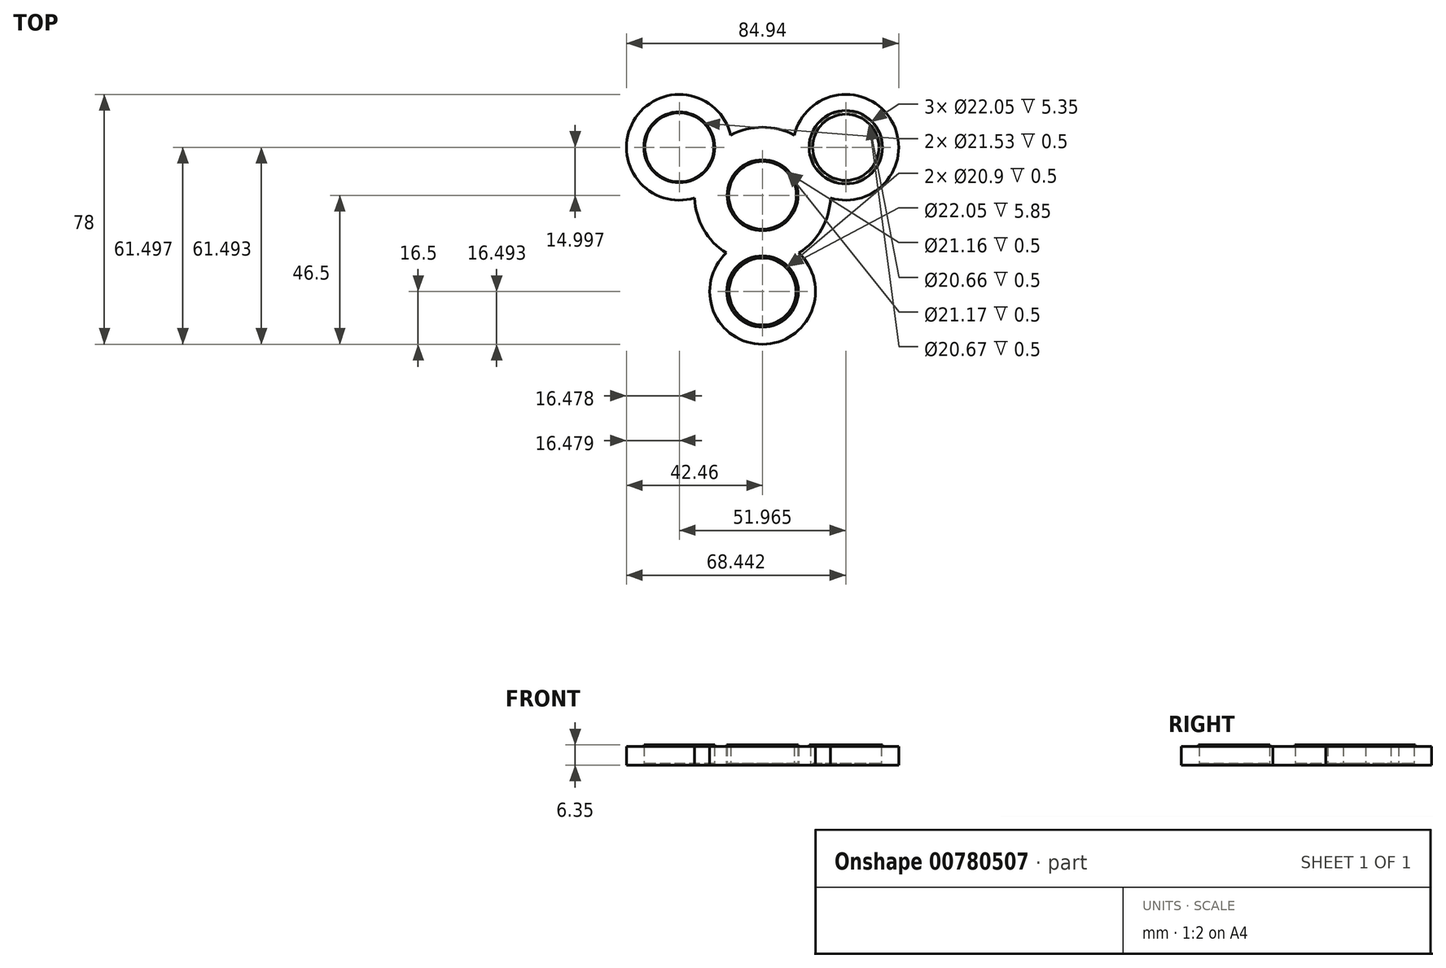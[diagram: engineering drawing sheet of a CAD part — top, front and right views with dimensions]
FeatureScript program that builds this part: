
annotation { "Feature Type Name" : "Feature", "Feature Type Description" : "" }
export const myFeature = defineFeature(function(context is Context, id is Id, definition is map)
    precondition{}
    {
        {
            var Q0;
            Q0=qCreatedBy(makeId("Top.planeOp"),FACE);
            var sketch = newSketch(context, id + "F0", { "sketchPlane" : qUnion([Q0])});
            skCircle(sketch, "E0", {"center": v(-25.96, 14.97) * mm, "radius": 16.5 * mm});
            skCircle(sketch, "E1", {"center": v(25.98, 15) * mm, "radius": 16.5 * mm});
            skCircle(sketch, "E2", {"center": v(0, -30) * mm, "radius": 16.5 * mm});
            skArc(sketch, "E3", {"start": v(-21.23, -0.84) * mm, "mid": v(-18.39, -10.63) * mm, "end": v(-11.31, -17.98) * mm});
            skArc(sketch, "E4.trimOffspring", {"start": v(11.31, -17.98) * mm, "mid": v(18.4, -10.62) * mm, "end": v(21.23, -0.8) * mm});
            skArc(sketch, "E5.trimOffspring", {"start": v(9.92, 18.78) * mm, "mid": v(0, 21.24) * mm, "end": v(-9.91, 18.79) * mm});
            skSolve(sketch);
        }
        {
            var Q0;
            Q0=qCreatedBy(makeId("Top.planeOp"),FACE);
            var sketch = newSketch(context, id + "F1", { "sketchPlane" : qUnion([Q0])});
            skCircle(sketch, "E6", {"center": v(0, 0) * mm, "radius": 11.03 * mm});
            skCircle(sketch, "E7", {"center": v(25.98, 15) * mm, "radius": 11.03 * mm});
            skCircle(sketch, "E8", {"center": v(-25.98, 15) * mm, "radius": 11.03 * mm});
            skCircle(sketch, "E9", {"center": v(0, -30) * mm, "radius": 11.03 * mm});
            skSolve(sketch);
        }
        {
            var Q0;
            Q0 = qSketchRegion(id + "F0", true);
            extrude(context, id + "F2", {"entities" : qUnion([Q0]), "depth" : 5.85 * mm, "offsetDistance" : 25 * mm});
        }
        {
            var Q0;
            Q0 = qSketchRegion(id + "F1", true);
            extrude(context, id + "F3", {"entities" : qUnion([Q0]), "operationType" : NewBodyOperationType.REMOVE, "depth" : 6.85 * mm, "offsetDistance" : 25 * mm});
        }
        {
            var Q0;
            Q0=makeQuery(id+"F1.imprint","IMPRINT",FACE,{"disambiguationData":[TD([[makeQuery(id+"F1.imprint","IMPRINT",EDGE,{"derivedFrom":sQuery(id+"F1.wireOp",EDGE,"E8")}),1.0]])]});
            var sketch = newSketch(context, id + "F4", { "sketchPlane" : qUnion([Q0])});
            skCircle(sketch, "E10", {"center": v(-25.98, 15) * mm, "radius": 11.04 * mm});
            skCircle(sketch, "E11", {"center": v(-25.98, 15) * mm, "radius": 10.76 * mm});
            skSolve(sketch);
        }
        {
            var Q0;
            Q0 = qSketchRegion(id + "F4", true);
            extrude(context, id + "F5", {"entities" : qUnion([Q0]), "operationType" : NewBodyOperationType.ADD, "depth" : .5 * mm, "offsetDistance" : 25 * mm});
        }
        {
            var Q0;
            Q0=makeQuery(id+"F1.imprint","IMPRINT",FACE,{"disambiguationData":[TD([[makeQuery(id+"F1.imprint","IMPRINT",EDGE,{"derivedFrom":sQuery(id+"F1.wireOp",EDGE,"E6")}),1.0]])]});
            var sketch = newSketch(context, id + "F6", { "sketchPlane" : qUnion([Q0])});
            skCircle(sketch, "E12", {"center": v(0, 0) * mm, "radius": 11.04 * mm});
            skCircle(sketch, "E13", {"center": v(0, 0) * mm, "radius": 10.58 * mm});
            skSolve(sketch);
        }
        {
            var Q0;
            Q0 = qSketchRegion(id + "F6", true);
            extrude(context, id + "F7", {"entities" : qUnion([Q0]), "operationType" : NewBodyOperationType.ADD, "depth" : .5 * mm, "offsetDistance" : 25 * mm});
        }
        {
            var Q0;
            Q0=makeQuery(id+"F1.imprint","IMPRINT",FACE,{"disambiguationData":[TD([[makeQuery(id+"F1.imprint","IMPRINT",EDGE,{"derivedFrom":sQuery(id+"F1.wireOp",EDGE,"E7")}),1.0]])]});
            var sketch = newSketch(context, id + "F8", { "sketchPlane" : qUnion([Q0])});
            skCircle(sketch, "E14", {"center": v(25.98, 15) * mm, "radius": 11.03 * mm});
            skCircle(sketch, "E15", {"center": v(25.98, 15) * mm, "radius": 10.33 * mm});
            skSolve(sketch);
        }
        {
            var Q0;
            Q0 = qSketchRegion(id + "F8", true);
            extrude(context, id + "F9", {"entities" : qUnion([Q0]), "operationType" : NewBodyOperationType.ADD, "depth" : .5 * mm, "offsetDistance" : 25 * mm});
        }
        {
            var Q0;
            Q0=makeQuery(id+"F1.imprint","IMPRINT",FACE,{"disambiguationData":[TD([[makeQuery(id+"F1.imprint","IMPRINT",EDGE,{"derivedFrom":sQuery(id+"F1.wireOp",EDGE,"E9")}),1.0]])]});
            var sketch = newSketch(context, id + "F10", { "sketchPlane" : qUnion([Q0])});
            skCircle(sketch, "E16", {"center": v(0, -30) * mm, "radius": 11.02 * mm});
            skCircle(sketch, "E17", {"center": v(0, -30) * mm, "radius": 10.45 * mm});
            skSolve(sketch);
        }
        {
            var Q0;
            Q0 = qSketchRegion(id + "F10", true);
            extrude(context, id + "F11", {"entities" : qUnion([Q0]), "operationType" : NewBodyOperationType.ADD, "depth" : .5 * mm, "offsetDistance" : 25 * mm});
        }
        {
            var Q0;
            Q0=makeQuery(id+"F2.opExtrude","CAP_FACE",FACE,{"disambiguationData":[OSD([sQuery(id+"F0.wireOp",EDGE,"E0"),sQuery(id+"F0.wireOp",EDGE,"E1"),sQuery(id+"F0.wireOp",EDGE,"E2"),sQuery(id+"F0.wireOp",EDGE,"E3"),sQuery(id+"F0.wireOp",EDGE,"E4.trimOffspring"),sQuery(id+"F0.wireOp",EDGE,"E5.trimOffspring")])],"isStart":false});
            var sketch = newSketch(context, id + "F12", { "sketchPlane" : qUnion([Q0])});
            skCircle(sketch, "E18.0", {"center": v(-25.98, 15) * mm, "radius": 11.05 * mm});
            skCircle(sketch, "E19.0", {"center": v(-25.98, 15) * mm, "radius": 10.76 * mm});
            skCircle(sketch, "E20.0", {"center": v(25.98, 15) * mm, "radius": 10.33 * mm});
            skCircle(sketch, "E21.0", {"center": v(0, 0) * mm, "radius": 10.58 * mm});
            skCircle(sketch, "E22.0", {"center": v(0, -30) * mm, "radius": 10.45 * mm});
            skCircle(sketch, "E23", {"center": v(0, 0) * mm, "radius": 11.06 * mm});
            skCircle(sketch, "E24", {"center": v(25.98, 15) * mm, "radius": 11.46 * mm});
            skCircle(sketch, "E25", {"center": v(25.98, 15) * mm, "radius": 10.34 * mm});
            skCircle(sketch, "E26", {"center": v(0, -30) * mm, "radius": 11.16 * mm});
            skSolve(sketch);
        }
        {
            var Q0;
            Q0 = qSketchRegion(id + "F12", true);
            extrude(context, id + "F13", {"entities" : qUnion([Q0]), "operationType" : NewBodyOperationType.ADD, "depth" : .5 * mm, "offsetDistance" : 25 * mm});
        }
    });
